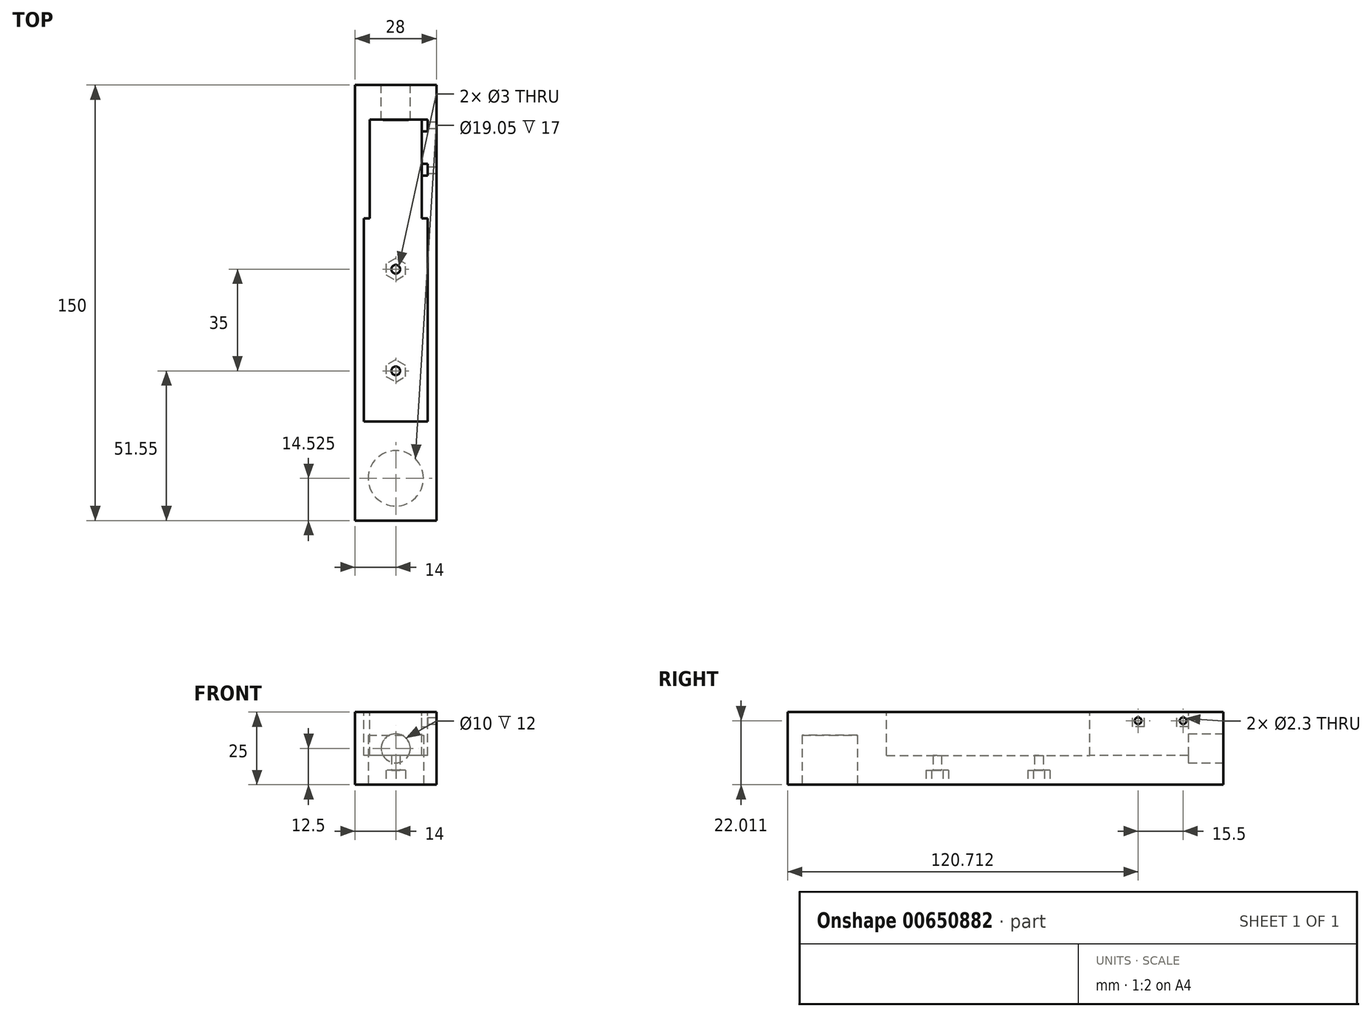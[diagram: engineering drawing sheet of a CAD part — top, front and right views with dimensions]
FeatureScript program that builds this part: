
annotation { "Feature Type Name" : "Feature", "Feature Type Description" : "" }
export const myFeature = defineFeature(function(context is Context, id is Id, definition is map)
    precondition{}
    {
        {
            var Q0;
            Q0=qCreatedBy(makeId("Front.planeOp"),FACE);
            var sketch = newSketch(context, id + "F0", { "sketchPlane" : qUnion([Q0])});
            skLineSegment(sketch, "E0.bottom", {"start": v(-14, 12.5) * mm, "end": v(14, 12.5) * mm});
            skLineSegment(sketch, "E0.top", {"start": v(-14, -12.5) * mm, "end": v(14, -12.5) * mm});
            skLineSegment(sketch, "E0.left", {"start": v(-14, 12.5) * mm, "end": v(-14, -12.5) * mm});
            skLineSegment(sketch, "E0.right", {"start": v(14, 12.5) * mm, "end": v(14, -12.5) * mm});
            skSolve(sketch);
        }
        {
            var Q0;
            Q0=makeQuery(id+"F0.imprint","IMPRINT",FACE,{"disambiguationData":[TD([[makeQuery(id+"F0.imprint","IMPRINT",EDGE,{"derivedFrom":sQuery(id+"F0.wireOp",EDGE,"E0.bottom")}),-1.0]])]});
            extrude(context, id + "F1", {"entities" : qUnion([Q0]), "oppositeDirection" : true, "depth" : 150 * mm, "offsetDistance" : 25 * mm});
        }
        {
            var Q0;
            Q0=makeQuery(id+"F1.opExtrude","SWEPT_FACE",FACE,{"disambiguationData":[OSD([sQuery(id+"F0.wireOp",EDGE,"E0.top")])]});
            var sketch = newSketch(context, id + "F2", { "sketchPlane" : qUnion([Q0])});
            skCircle(sketch, "E1", {"center": v(0, -14.53) * mm, "radius": 9.53 * mm});
            skSolve(sketch);
        }
        {
            var Q0;
            Q0 = qSketchRegion(id + "F2", true);
            extrude(context, id + "F3", {"entities" : qUnion([Q0]), "operationType" : NewBodyOperationType.REMOVE, "oppositeDirection" : true, "depth" : 17 * mm, "offsetDistance" : 25 * mm});
        }
        {
            var Q0;
            Q0=makeQuery(id+"F1.opExtrude","SWEPT_FACE",FACE,{"disambiguationData":[OSD([sQuery(id+"F0.wireOp",EDGE,"E0.top")])]});
            var sketch = newSketch(context, id + "F4", { "sketchPlane" : qUnion([Q0])});
            skCircle(sketch, "E2", {"center": v(0, -51.55) * mm, "radius": 3.32 * mm});
            skCircle(sketch, "E3.cCircle", {"center": v(0, -51.55) * mm, "radius": 3.32 * mm, "construction": true});
            skLineSegment(sketch, "E3.0", {"start": v(3.32, -49.63) * mm, "end": v(3.32, -53.47) * mm});
            skLineSegment(sketch, "E3.1", {"start": v(3.32, -53.47) * mm, "end": v(0, -55.38) * mm});
            skLineSegment(sketch, "E3.2", {"start": v(0, -55.38) * mm, "end": v(-3.32, -53.47) * mm});
            skLineSegment(sketch, "E3.3", {"start": v(-3.32, -53.47) * mm, "end": v(-3.32, -49.63) * mm});
            skLineSegment(sketch, "E3.4", {"start": v(-3.32, -49.63) * mm, "end": v(0, -47.72) * mm});
            skLineSegment(sketch, "E3.5", {"start": v(0, -47.72) * mm, "end": v(3.32, -49.63) * mm});
            skPoint(sketch, "E3.0.midPoint", {"position": v(3.32, -51.55) * mm});
            skCircle(sketch, "E4", {"center": v(0, -51.55) * mm, "radius": 1.5 * mm});
            skCircle(sketch, "E5", {"center": v(0, -86.55) * mm, "radius": 3.32 * mm});
            skCircle(sketch, "E6.cCircle", {"center": v(0, -86.55) * mm, "radius": 3.32 * mm, "construction": true});
            skLineSegment(sketch, "E6.0", {"start": v(3.32, -84.63) * mm, "end": v(3.32, -88.47) * mm});
            skLineSegment(sketch, "E6.1", {"start": v(3.32, -88.47) * mm, "end": v(0, -90.38) * mm});
            skLineSegment(sketch, "E6.2", {"start": v(0, -90.38) * mm, "end": v(-3.32, -88.47) * mm});
            skLineSegment(sketch, "E6.3", {"start": v(-3.32, -88.47) * mm, "end": v(-3.32, -84.63) * mm});
            skLineSegment(sketch, "E6.4", {"start": v(-3.32, -84.63) * mm, "end": v(0, -82.72) * mm});
            skLineSegment(sketch, "E6.5", {"start": v(0, -82.72) * mm, "end": v(3.32, -84.63) * mm});
            skPoint(sketch, "E6.0.midPoint", {"position": v(3.32, -86.55) * mm});
            skCircle(sketch, "E7", {"center": v(0, -86.55) * mm, "radius": 1.5 * mm});
            skSolve(sketch);
        }
        {
            var Q0;
            Q0 = qSketchRegion(id + "F4", true);
            extrude(context, id + "F5", {"entities" : qUnion([Q0]), "operationType" : NewBodyOperationType.REMOVE, "oppositeDirection" : true, "depth" : 5 * mm, "offsetDistance" : 25 * mm});
        }
        {
            var Q0;
            {var subQ1=sQuery(id+"F0.wireOp",EDGE,"E0.left");var subQ2=sQuery(id+"F0.wireOp",EDGE,"E0.top");Q0=makeQuery(id+"F5.boolean.opBoolean","SPLIT",FACE,{"disambiguationData":[TD([makeQuery(id+"F1.opExtrude","SWEPT_FACE",FACE,{"disambiguationData":[OSD([subQ1])]})])],"derivedFrom":makeQuery(id+"F1.opExtrude","SWEPT_FACE",FACE,{"disambiguationData":[OSD([subQ2])]})});}
            var sketch = newSketch(context, id + "F6", { "sketchPlane" : qUnion([Q0])});
            skCircle(sketch, "E8", {"center": v(0, -51.55) * mm, "radius": 1.5 * mm});
            skPoint(sketch, "E8.centerSnap0", {"position": v(3.32, -51.55) * mm});
            skCircle(sketch, "E9", {"center": v(0, -86.55) * mm, "radius": 1.5 * mm});
            skPoint(sketch, "E9.centerSnap0", {"position": v(-3.32, -86.55) * mm});
            skSolve(sketch);
        }
        {
            var Q0;
            Q0 = qSketchRegion(id + "F6", true);
            extrude(context, id + "F7", {"entities" : qUnion([Q0]), "operationType" : NewBodyOperationType.REMOVE, "endBound" : BoundingType.THROUGH_ALL, "oppositeDirection" : true, "depth" : 25 * mm, "offsetDistance" : 25 * mm});
        }
        {
            var Q0;
            Q0=makeQuery(id+"F1.opExtrude","SWEPT_FACE",FACE,{"disambiguationData":[OSD([sQuery(id+"F0.wireOp",EDGE,"E0.bottom")])]});
            var sketch = newSketch(context, id + "F8", { "sketchPlane" : qUnion([Q0])});
            skLineSegment(sketch, "E10.bottom", {"start": v(11, 34.05) * mm, "end": v(-11, 34.05) * mm});
            skLineSegment(sketch, "E10.top", {"start": v(11, 104.05) * mm, "end": v(-11, 104.05) * mm});
            skLineSegment(sketch, "E10.left", {"start": v(11, 34.05) * mm, "end": v(11, 104.05) * mm});
            skLineSegment(sketch, "E10.right", {"start": v(-11, 34.05) * mm, "end": v(-11, 104.05) * mm});
            skSolve(sketch);
        }
        {
            var Q0;
            Q0 = qSketchRegion(id + "F8", true);
            extrude(context, id + "F9", {"entities" : qUnion([Q0]), "operationType" : NewBodyOperationType.REMOVE, "oppositeDirection" : true, "depth" : 15 * mm, "offsetDistance" : 25 * mm});
        }
        {
            var Q0;
            Q0=makeQuery(id+"F1.opExtrude","SWEPT_FACE",FACE,{"disambiguationData":[OSD([sQuery(id+"F0.wireOp",EDGE,"E0.right")])]});
            var sketch = newSketch(context, id + "F10", { "sketchPlane" : qUnion([Q0])});
            skCircle(sketch, "E11", {"center": v(120.71, 9.51) * mm, "radius": 1.15 * mm});
            skCircle(sketch, "E12", {"center": v(136.21, 9.51) * mm, "radius": 1.15 * mm});
            skLineSegment(sketch, "E13.bottom", {"start": v(118.96, 11.66) * mm, "end": v(137.96, 11.66) * mm});
            skLineSegment(sketch, "E13.top", {"start": v(118.96, 7.36) * mm, "end": v(137.96, 7.36) * mm});
            skLineSegment(sketch, "E13.left", {"start": v(118.96, 11.66) * mm, "end": v(118.96, 7.36) * mm});
            skLineSegment(sketch, "E13.right", {"start": v(137.96, 11.66) * mm, "end": v(137.96, 7.36) * mm});
            skLineSegment(sketch, "E14.bottom", {"start": v(122.87, 12.5) * mm, "end": v(134.06, 12.5) * mm});
            skLineSegment(sketch, "E14.top", {"start": v(122.87, 6.61) * mm, "end": v(134.06, 6.61) * mm});
            skLineSegment(sketch, "E14.left", {"start": v(122.87, 12.5) * mm, "end": v(122.87, 6.61) * mm});
            skLineSegment(sketch, "E14.right", {"start": v(134.06, 12.5) * mm, "end": v(134.06, 6.61) * mm});
            skSolve(sketch);
        }
        {
            var Q0;
            Q0=makeQuery(id+"F10.imprint","IMPRINT",FACE,{"disambiguationData":[TD([[makeQuery(id+"F10.imprint","IMPRINT",EDGE,{"derivedFrom":sQuery(id+"F10.wireOp",EDGE,"E12")}),1.0]])]});
            var Q1;
            Q1=makeQuery(id+"F10.imprint","IMPRINT",FACE,{"disambiguationData":[TD([[makeQuery(id+"F10.imprint","IMPRINT",EDGE,{"derivedFrom":sQuery(id+"F10.wireOp",EDGE,"E11")}),1.0]])]});
            extrude(context, id + "F11", {"entities" : qUnion([Q0, Q1]), "operationType" : NewBodyOperationType.REMOVE, "oppositeDirection" : true, "depth" : 5 * mm, "offsetDistance" : 25 * mm});
        }
        {
            var Q0;
            Q0=makeQuery(id+"F8.imprint","IMPRINT",FACE,{"disambiguationData":[TD([[makeQuery(id+"F8.imprint","IMPRINT",EDGE,{"derivedFrom":sQuery(id+"F8.wireOp",EDGE,"E10.bottom")}),1.0]])]});
            var sketch = newSketch(context, id + "F12", { "sketchPlane" : qUnion([Q0])});
            skLineSegment(sketch, "E15.bottom", {"start": v(9, 122.84) * mm, "end": v(11, 122.84) * mm});
            skLineSegment(sketch, "E15.top", {"start": v(9, 118.82) * mm, "end": v(11, 118.82) * mm});
            skLineSegment(sketch, "E15.left", {"start": v(9, 122.84) * mm, "end": v(9, 118.82) * mm});
            skLineSegment(sketch, "E15.right", {"start": v(11, 122.84) * mm, "end": v(11, 118.82) * mm});
            skLineSegment(sketch, "E16.bottom", {"start": v(9, 138.1) * mm, "end": v(11, 138.1) * mm});
            skLineSegment(sketch, "E16.top", {"start": v(9, 134.07) * mm, "end": v(11, 134.07) * mm});
            skLineSegment(sketch, "E16.left", {"start": v(9, 138.1) * mm, "end": v(9, 134.07) * mm});
            skLineSegment(sketch, "E16.right", {"start": v(11, 138.1) * mm, "end": v(11, 134.07) * mm});
            skSolve(sketch);
        }
        {
            var Q0;
            Q0 = qSketchRegion(id + "F12", true);
            extrude(context, id + "F13", {"entities" : qUnion([Q0]), "operationType" : NewBodyOperationType.REMOVE, "oppositeDirection" : true, "depth" : 5 * mm, "offsetDistance" : 25 * mm});
        }
        {
            var Q0;
            Q0=makeQuery(id+"F8.imprint","IMPRINT",FACE,{"disambiguationData":[TD([[makeQuery(id+"F8.imprint","IMPRINT",EDGE,{"derivedFrom":sQuery(id+"F8.wireOp",EDGE,"E10.bottom")}),1.0]])]});
            var sketch = newSketch(context, id + "F14", { "sketchPlane" : qUnion([Q0])});
            skLineSegment(sketch, "E17.bottom", {"start": v(9, 138.1) * mm, "end": v(-9, 138.1) * mm});
            skLineSegment(sketch, "E17.top", {"start": v(9, 118.82) * mm, "end": v(-9, 118.82) * mm});
            skLineSegment(sketch, "E17.left", {"start": v(9, 138.1) * mm, "end": v(9, 118.82) * mm});
            skLineSegment(sketch, "E17.right", {"start": v(-9, 138.1) * mm, "end": v(-9, 118.82) * mm});
            skSolve(sketch);
        }
        {
            var Q0;
            Q0 = qSketchRegion(id + "F14", true);
            extrude(context, id + "F15", {"entities" : qUnion([Q0]), "operationType" : NewBodyOperationType.REMOVE, "oppositeDirection" : true, "depth" : 15 * mm, "offsetDistance" : 25 * mm});
        }
        {
            var Q0;
            Q0=makeQuery(id+"F14.imprint","IMPRINT",FACE,{"disambiguationData":[TD([[makeQuery(id+"F14.imprint","IMPRINT",EDGE,{"derivedFrom":sQuery(id+"F14.wireOp",EDGE,"E17.bottom")}),-1.0]])]});
            var sketch = newSketch(context, id + "F16", { "sketchPlane" : qUnion([Q0])});
            skLineSegment(sketch, "E18.bottom", {"start": v(9, 118.82) * mm, "end": v(-9, 118.82) * mm});
            skLineSegment(sketch, "E18.top", {"start": v(9, 104.05) * mm, "end": v(-9, 104.05) * mm});
            skLineSegment(sketch, "E18.left", {"start": v(9, 118.82) * mm, "end": v(9, 104.05) * mm});
            skLineSegment(sketch, "E18.right", {"start": v(-9, 118.82) * mm, "end": v(-9, 104.05) * mm});
            skSolve(sketch);
        }
        {
            var Q0;
            Q0 = qSketchRegion(id + "F16", true);
            extrude(context, id + "F17", {"entities" : qUnion([Q0]), "operationType" : NewBodyOperationType.REMOVE, "oppositeDirection" : true, "depth" : 15 * mm, "offsetDistance" : 25 * mm});
        }
        {
            var Q0;
            Q0=makeQuery(id+"F1.opExtrude","CAP_FACE",FACE,{"disambiguationData":[OSD([sQuery(id+"F0.wireOp",EDGE,"E0.bottom"),sQuery(id+"F0.wireOp",EDGE,"E0.top"),sQuery(id+"F0.wireOp",EDGE,"E0.left"),sQuery(id+"F0.wireOp",EDGE,"E0.right")])],"isStart":false});
            var sketch = newSketch(context, id + "F18", { "sketchPlane" : qUnion([Q0])});
            skCircle(sketch, "E19", {"center": v(0, 0) * mm, "radius": 5 * mm});
            skSolve(sketch);
        }
        {
            var Q0;
            Q0 = qSketchRegion(id + "F18", true);
            extrude(context, id + "F19", {"entities" : qUnion([Q0]), "operationType" : NewBodyOperationType.REMOVE, "oppositeDirection" : true, "depth" : 12 * mm, "offsetDistance" : 25 * mm});
        }
        {
            var Q0;
            Q0=sQuery(id+"F10.wireOp",EDGE,"E14.right");
            var Q1;
            Q1=sQuery(id+"F10.wireOp",EDGE,"E14.left");
            var Q2;
            Q2=sQuery(id+"F10.wireOp",EDGE,"E14.top");
            var Q3;
            Q3=sQuery(id+"F10.wireOp",EDGE,"E14.bottom");
            extrude(context, id + "F20", {"bodyType" : ToolBodyType.SURFACE, "surfaceEntities" : qUnion([Q0, Q1, Q2, Q3]), "oppositeDirection" : true, "depth" : 10 * mm, "offsetDistance" : 25 * mm});
        }
    });
